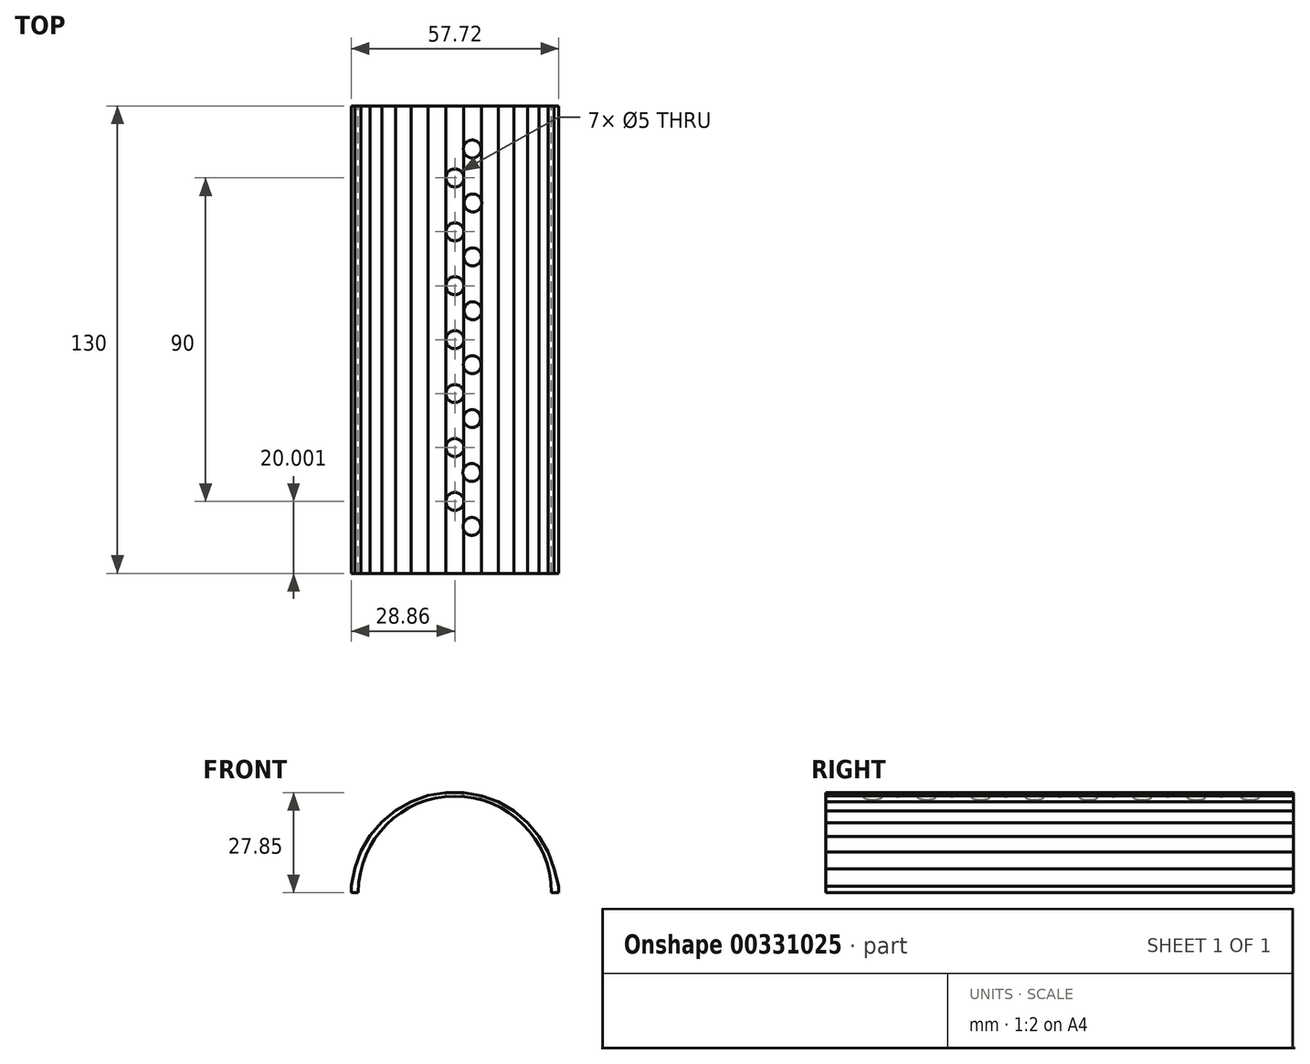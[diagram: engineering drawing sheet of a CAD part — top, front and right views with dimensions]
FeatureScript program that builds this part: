
annotation { "Feature Type Name" : "Feature", "Feature Type Description" : "" }
export const myFeature = defineFeature(function(context is Context, id is Id, definition is map)
    precondition{}
    {
        {
            var Q0;
            Q0=qCreatedBy(makeId("Front.planeOp"),FACE);
            var sketch = newSketch(context, id + "F0", { "sketchPlane" : qUnion([Q0])});
            skLineSegment(sketch, "E0.7", {"start": v(-28.86, 1.96) * mm, "end": v(-27.83, 6.85) * mm});
            skLineSegment(sketch, "E0.8", {"start": v(-27.83, 6.85) * mm, "end": v(-26.1, 11.54) * mm});
            skLineSegment(sketch, "E0.9", {"start": v(-26.1, 11.54) * mm, "end": v(-23.57, 15.85) * mm});
            skLineSegment(sketch, "E0.10", {"start": v(-23.57, 15.85) * mm, "end": v(-20.33, 19.66) * mm});
            skLineSegment(sketch, "E0.11", {"start": v(-20.33, 19.66) * mm, "end": v(-16.48, 22.85) * mm});
            skLineSegment(sketch, "E0.12", {"start": v(-16.48, 22.85) * mm, "end": v(-12.14, 25.33) * mm});
            skLineSegment(sketch, "E0.13", {"start": v(-12.14, 25.33) * mm, "end": v(-7.43, 27.01) * mm});
            skLineSegment(sketch, "E0.14", {"start": v(-7.43, 27.01) * mm, "end": v(-2.5, 27.85) * mm});
            skLineSegment(sketch, "E0.15", {"start": v(-2.5, 27.85) * mm, "end": v(2.5, 27.85) * mm});
            skLineSegment(sketch, "E0.16", {"start": v(2.5, 27.85) * mm, "end": v(7.42, 26.98) * mm});
            skLineSegment(sketch, "E0.17", {"start": v(7.42, 26.98) * mm, "end": v(12.11, 25.25) * mm});
            skLineSegment(sketch, "E0.18", {"start": v(12.11, 25.25) * mm, "end": v(16.43, 22.72) * mm});
            skLineSegment(sketch, "E0.19", {"start": v(16.43, 22.72) * mm, "end": v(20.24, 19.49) * mm});
            skLineSegment(sketch, "E0.20", {"start": v(20.24, 19.49) * mm, "end": v(23.43, 15.64) * mm});
            skLineSegment(sketch, "E0.21", {"start": v(23.43, 15.64) * mm, "end": v(25.9, 11.3) * mm});
            skLineSegment(sketch, "E0.22", {"start": v(25.9, 11.3) * mm, "end": v(27.59, 6.58) * mm});
            skLineSegment(sketch, "E0.23", {"start": v(27.59, 6.58) * mm, "end": v(28.86, 1.75) * mm});
            skLineSegment(sketch, "E1", {"start": v(28.86, 1.75) * mm, "end": v(28.86, 0) * mm});
            skLineSegment(sketch, "E2", {"start": v(-28.86, 1.96) * mm, "end": v(-28.86, 0) * mm});
            skArc(sketch, "E3", {"start": v(26.86, 0) * mm, "mid": v(0, 26.86) * mm, "end": v(-26.86, 0) * mm});
            skLineSegment(sketch, "E4", {"start": v(28.86, 0) * mm, "end": v(26.86, 0) * mm});
            skLineSegment(sketch, "E5", {"start": v(-26.86, 0) * mm, "end": v(-28.86, 0) * mm});
            skSolve(sketch);
        }
        {
            var Q0;
            Q0=makeQuery(id+"F0.imprint","IMPRINT",FACE,{"disambiguationData":[TD([[makeQuery(id+"F0.imprint","IMPRINT",EDGE,{"derivedFrom":sQuery(id+"F0.wireOp",EDGE,"E0.7")}),-1.0]])]});
            extrude(context, id + "F1", {"entities" : qUnion([Q0]), "depth" : 130 * mm});
        }
        {
            var Q0;
            Q0=makeQuery(id+"F1.opExtrude","SWEPT_FACE",FACE,{"disambiguationData":[OSD([sQuery(id+"F0.wireOp",EDGE,"E0.15")])]});
            var sketch = newSketch(context, id + "F2", { "sketchPlane" : qUnion([Q0])});
            skCircle(sketch, "E6", {"center": v(0, -20) * mm, "radius": 2.5 * mm});
            skCircle(sketch, "E7", {"center": v(0, -50) * mm, "radius": 2.5 * mm});
            skCircle(sketch, "E8", {"center": v(0, -65) * mm, "radius": 2.5 * mm});
            skCircle(sketch, "E9", {"center": v(0, -80) * mm, "radius": 2.5 * mm});
            skCircle(sketch, "E10", {"center": v(0, -95) * mm, "radius": 2.5 * mm});
            skCircle(sketch, "E11", {"center": v(0, -110) * mm, "radius": 2.5 * mm});
            skCircle(sketch, "E12", {"center": v(0, -35) * mm, "radius": 2.5 * mm});
            skSolve(sketch);
        }
        {
            var Q0;
            Q0=sQuery(id+"F2.wireOp",VERTEX,"E6.center");
            var Q1;
            Q1=sQuery(id+"F2.wireOp",VERTEX,"E12.center");
            var Q2;
            Q2=sQuery(id+"F2.wireOp",VERTEX,"E7.center");
            var Q3;
            Q3=sQuery(id+"F2.wireOp",VERTEX,"E8.center");
            var Q4;
            Q4=sQuery(id+"F2.wireOp",VERTEX,"E9.center");
            var Q5;
            Q5=sQuery(id+"F2.wireOp",VERTEX,"E10.center");
            var Q6;
            Q6=sQuery(id+"F2.wireOp",VERTEX,"E11.center");
            var Q7;
            Q7=makeQuery(id+"F1.opExtrude","SWEPT_BODY",BODY,{"disambiguationData":[OSD([sQuery(id+"F0.wireOp",EDGE,"E0.7"),sQuery(id+"F0.wireOp",EDGE,"E0.8"),sQuery(id+"F0.wireOp",EDGE,"E0.9"),sQuery(id+"F0.wireOp",EDGE,"E0.10"),sQuery(id+"F0.wireOp",EDGE,"E0.11"),sQuery(id+"F0.wireOp",EDGE,"E0.12"),sQuery(id+"F0.wireOp",EDGE,"E0.13"),sQuery(id+"F0.wireOp",EDGE,"E0.14"),sQuery(id+"F0.wireOp",EDGE,"E0.15"),sQuery(id+"F0.wireOp",EDGE,"E0.16"),sQuery(id+"F0.wireOp",EDGE,"E0.17"),sQuery(id+"F0.wireOp",EDGE,"E0.18"),sQuery(id+"F0.wireOp",EDGE,"E0.19"),sQuery(id+"F0.wireOp",EDGE,"E0.20"),sQuery(id+"F0.wireOp",EDGE,"E0.21"),sQuery(id+"F0.wireOp",EDGE,"E0.22"),sQuery(id+"F0.wireOp",EDGE,"E0.23"),sQuery(id+"F0.wireOp",EDGE,"E1"),sQuery(id+"F0.wireOp",EDGE,"E2"),sQuery(id+"F0.wireOp",EDGE,"E3"),sQuery(id+"F0.wireOp",EDGE,"E4"),sQuery(id+"F0.wireOp",EDGE,"E5")])]});
            hole(context, id + "F3", {"style" : HoleStyle.SIMPLE, "endStyle" : HoleEndStyle.THROUGH, "holeDiameter" : 5 * mm, "tappedDepth" : 12 * mm, "tapClearance" : 3, "locations" : qUnion([Q0, Q1, Q2, Q3, Q4, Q5, Q6]), "scope" : qUnion([Q7])});
        }
        {
            var Q0;
            Q0=makeQuery(id+"F1.opExtrude","SWEPT_FACE",FACE,{"disambiguationData":[OSD([sQuery(id+"F0.wireOp",EDGE,"E0.16")])]});
            var sketch = newSketch(context, id + "F4", { "sketchPlane" : qUnion([Q0])});
            skCircle(sketch, "E13", {"center": v(0.17, -26.96) * mm, "radius": 2.5 * mm});
            skCircle(sketch, "E14", {"center": v(0.11, -41.96) * mm, "radius": 2.5 * mm});
            skCircle(sketch, "E15", {"center": v(0.15, -56.96) * mm, "radius": 2.5 * mm});
            skCircle(sketch, "E16", {"center": v(0, -71.96) * mm, "radius": 2.5 * mm});
            skCircle(sketch, "E17", {"center": v(0, -86.96) * mm, "radius": 2.5 * mm});
            skCircle(sketch, "E18", {"center": v(-0.14, -101.96) * mm, "radius": 2.5 * mm});
            skCircle(sketch, "E19", {"center": v(-0.1, -116.96) * mm, "radius": 2.5 * mm});
            skCircle(sketch, "E20", {"center": v(0, -11.96) * mm, "radius": 2.5 * mm});
            skSolve(sketch);
        }
        {
            var Q0;
            Q0=sQuery(id+"F4.wireOp",VERTEX,"E19.center");
            var Q1;
            Q1=sQuery(id+"F4.wireOp",VERTEX,"E18.center");
            var Q2;
            Q2=sQuery(id+"F4.wireOp",VERTEX,"E17.center");
            var Q3;
            Q3=sQuery(id+"F4.wireOp",VERTEX,"E16.center");
            var Q4;
            Q4=sQuery(id+"F4.wireOp",VERTEX,"E15.center");
            var Q5;
            Q5=sQuery(id+"F4.wireOp",VERTEX,"E14.center");
            var Q6;
            Q6=sQuery(id+"F4.wireOp",VERTEX,"E13.center");
            var Q7;
            Q7=sQuery(id+"F4.wireOp",VERTEX,"E20.center");
            var Q8;
            Q8=makeQuery(id+"F1.opExtrude","SWEPT_BODY",BODY,{"disambiguationData":[OSD([sQuery(id+"F0.wireOp",EDGE,"E0.7"),sQuery(id+"F0.wireOp",EDGE,"E0.8"),sQuery(id+"F0.wireOp",EDGE,"E0.9"),sQuery(id+"F0.wireOp",EDGE,"E0.10"),sQuery(id+"F0.wireOp",EDGE,"E0.11"),sQuery(id+"F0.wireOp",EDGE,"E0.12"),sQuery(id+"F0.wireOp",EDGE,"E0.13"),sQuery(id+"F0.wireOp",EDGE,"E0.14"),sQuery(id+"F0.wireOp",EDGE,"E0.15"),sQuery(id+"F0.wireOp",EDGE,"E0.16"),sQuery(id+"F0.wireOp",EDGE,"E0.17"),sQuery(id+"F0.wireOp",EDGE,"E0.18"),sQuery(id+"F0.wireOp",EDGE,"E0.19"),sQuery(id+"F0.wireOp",EDGE,"E0.20"),sQuery(id+"F0.wireOp",EDGE,"E0.21"),sQuery(id+"F0.wireOp",EDGE,"E0.22"),sQuery(id+"F0.wireOp",EDGE,"E0.23"),sQuery(id+"F0.wireOp",EDGE,"E1"),sQuery(id+"F0.wireOp",EDGE,"E2"),sQuery(id+"F0.wireOp",EDGE,"E3"),sQuery(id+"F0.wireOp",EDGE,"E4"),sQuery(id+"F0.wireOp",EDGE,"E5")])]});
            hole(context, id + "F5", {"style" : HoleStyle.SIMPLE, "endStyle" : HoleEndStyle.THROUGH, "holeDiameter" : 5 * mm, "isTappedThrough" : true, "tappedDepth" : 12 * mm, "tapClearance" : 3, "locations" : qUnion([Q0, Q1, Q2, Q3, Q4, Q5, Q6, Q7]), "scope" : qUnion([Q8])});
        }
    });
